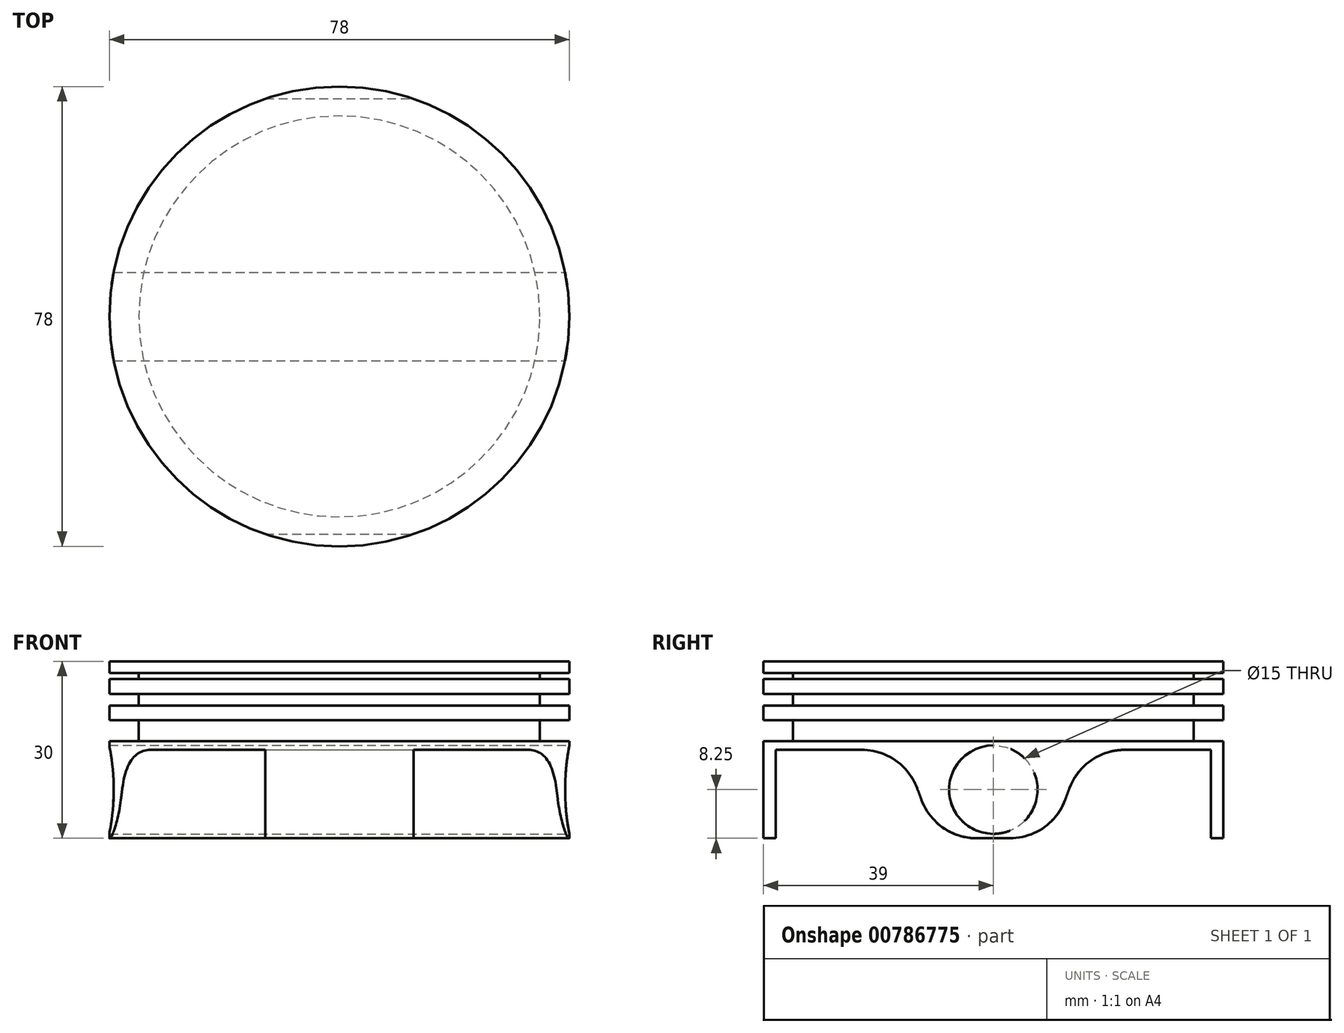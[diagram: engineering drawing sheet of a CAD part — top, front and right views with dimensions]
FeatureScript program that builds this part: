
annotation { "Feature Type Name" : "Feature", "Feature Type Description" : "" }
export const myFeature = defineFeature(function(context is Context, id is Id, definition is map)
    precondition{}
    {
        {
            var Q0;
            Q0=qCreatedBy(makeId("Front.planeOp"),FACE);
            var sketch = newSketch(context, id + "F0", { "sketchPlane" : qUnion([Q0])});
            skLineSegment(sketch, "E0", {"start": v(0, 30) * mm, "end": v(39, 30) * mm});
            skLineSegment(sketch, "E1", {"start": v(39, 30) * mm, "end": v(39, 28) * mm});
            skLineSegment(sketch, "E2", {"start": v(39, 28) * mm, "end": v(34, 28) * mm});
            skLineSegment(sketch, "E3", {"start": v(34, 28) * mm, "end": v(34, 27) * mm});
            skLineSegment(sketch, "E4", {"start": v(34, 27) * mm, "end": v(39, 27) * mm});
            skLineSegment(sketch, "E5", {"start": v(39, 27) * mm, "end": v(39, 24.5) * mm});
            skLineSegment(sketch, "E6", {"start": v(39, 24.5) * mm, "end": v(34, 24.5) * mm});
            skLineSegment(sketch, "E7", {"start": v(34, 24.5) * mm, "end": v(34, 22.5) * mm});
            skLineSegment(sketch, "E8", {"start": v(34, 22.5) * mm, "end": v(39, 22.5) * mm});
            skLineSegment(sketch, "E9", {"start": v(39, 22.5) * mm, "end": v(39, 20) * mm});
            skLineSegment(sketch, "E10", {"start": v(39, 20) * mm, "end": v(34, 20) * mm});
            skLineSegment(sketch, "E11", {"start": v(34, 20) * mm, "end": v(34, 16.5) * mm});
            skLineSegment(sketch, "E12", {"start": v(34, 16.5) * mm, "end": v(39, 16.5) * mm});
            skLineSegment(sketch, "E13", {"start": v(39, 16.5) * mm, "end": v(39, 0) * mm});
            skPoint(sketch, "E14.end.orphan", {"position": v(0.38, 15.14) * mm});
            skLineSegment(sketch, "E15", {"start": v(0, 30) * mm, "end": v(0, 0) * mm});
            skLineSegment(sketch, "E16", {"start": v(39, 0) * mm, "end": v(0, 0) * mm});
            skSolve(sketch);
        }
        {
            var Q0;
            Q0=makeQuery(id+"F0.imprint","IMPRINT",FACE,{"disambiguationData":[TD([[makeQuery(id+"F0.imprint","IMPRINT",EDGE,{"derivedFrom":sQuery(id+"F0.wireOp",EDGE,"E0")}),-1.0]])]});
            var Q1;
            Q1=sQuery(id+"F0.wireOp",EDGE,"E15");
            revolve(context, id + "F1", {"surfaceOperationType" : NewSurfaceOperationType.NEW, "entities" : qUnion([Q0]), "axis" : qUnion([Q1]), "revolveType" : RevolveType.FULL});
        }
        {
            var Q0;
            Q0=qCreatedBy(makeId("Right.planeOp"),FACE);
            var sketch = newSketch(context, id + "F2", { "sketchPlane" : qUnion([Q0])});
            skLineSegment(sketch, "E17", {"start": v(0, 0) * mm, "end": v(0, 15) * mm});
            skLineSegment(sketch, "E18", {"start": v(22.29, 15) * mm, "end": v(36.91, 15) * mm});
            skLineSegment(sketch, "E19", {"start": v(36.91, 15) * mm, "end": v(36.91, 0) * mm});
            skPoint(sketch, "E20.visualSharp", {"position": v(19.5, 15) * mm});
            skLineSegment(sketch, "E21", {"start": v(0, 0) * mm, "end": v(2.8, 0) * mm});
            skLineSegment(sketch, "E22", {"start": v(12.92, 8.5) * mm, "end": v(12.18, 6.5) * mm});
            skPoint(sketch, "E23.visualSharp", {"position": v(15.34, 15) * mm});
            skArc(sketch, "E23.filletArc", {"start": v(22.29, 15) * mm, "mid": v(16.58, 13.21) * mm, "end": v(12.92, 8.5) * mm});
            skArc(sketch, "E24.filletArc", {"start": v(2.8, 0) * mm, "mid": v(8.5, 1.79) * mm, "end": v(12.18, 6.5) * mm});
            skLineSegment(sketch, "E25", {"start": v(2.8, 0) * mm, "end": v(36.91, 0) * mm});
            skLineSegment(sketch, "E26.MirrorCS", {"start": v(0, 0) * mm, "end": v(-2.8, 0) * mm});
            skLineSegment(sketch, "E27.MirrorCS", {"start": v(-12.92, 8.5) * mm, "end": v(-12.18, 6.5) * mm});
            skArc(sketch, "E28.MirrorCS", {"start": v(-22.29, 15) * mm, "mid": v(-16.58, 13.21) * mm, "end": v(-12.92, 8.5) * mm});
            skArc(sketch, "E29.MirrorCS", {"start": v(-2.8, 0) * mm, "mid": v(-8.5, 1.79) * mm, "end": v(-12.18, 6.5) * mm});
            skPoint(sketch, "E30.MirrorP", {"position": v(-15.34, 15) * mm});
            skPoint(sketch, "E31.MirrorP", {"position": v(-19.5, 15) * mm});
            skLineSegment(sketch, "E32.MirrorCS", {"start": v(-36.91, 15) * mm, "end": v(-36.91, 0) * mm});
            skLineSegment(sketch, "E33.MirrorCS", {"start": v(-2.8, 0) * mm, "end": v(-36.91, 0) * mm});
            skLineSegment(sketch, "E34.MirrorCS", {"start": v(-22.29, 15) * mm, "end": v(-36.91, 15) * mm});
            skSolve(sketch);
        }
        {
            var Q0;
            Q0 = qSketchRegion(id + "F2", true);
            extrude(context, id + "F3", {"entities" : qUnion([Q0]), "operationType" : NewBodyOperationType.REMOVE, "endBound" : BoundingType.SYMMETRIC, "oppositeDirection" : true, "depth" : 100 * mm, "offsetDistance" : 25 * mm});
        }
        {
            var Q0;
            Q0=qCreatedBy(makeId("Right.planeOp"),FACE);
            var sketch = newSketch(context, id + "F4", { "sketchPlane" : qUnion([Q0])});
            skLineSegment(sketch, "E35", {"start": v(0, 0) * mm, "end": v(0, 16.5) * mm});
            skLineSegment(sketch, "E36", {"start": v(0, 8.25) * mm, "end": v(3.24, 8.25) * mm});
            skCircle(sketch, "E37", {"center": v(0, 8.25) * mm, "radius": 7.5 * mm});
            skSolve(sketch);
        }
        {
            var Q0;
            Q0 = qSketchRegion(id + "F4", true);
            extrude(context, id + "F5", {"entities" : qUnion([Q0]), "operationType" : NewBodyOperationType.REMOVE, "endBound" : BoundingType.SYMMETRIC, "oppositeDirection" : true, "depth" : 100 * mm, "offsetDistance" : 25 * mm});
        }
    });
